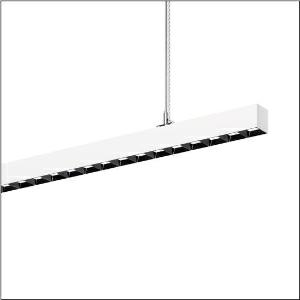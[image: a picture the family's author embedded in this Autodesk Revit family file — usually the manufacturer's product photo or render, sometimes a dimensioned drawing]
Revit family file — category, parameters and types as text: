
# Revit family: silica_r__21_51mx32dc3dwb_4ada
name_source: partatom
category: Lighting Fixtures
units: mm (PartAtom-declared; Revit-internal decimal feet)

## family parameters
Cut with Voids When Loaded = No
Host = Face
Light Source = No
Part Type = Normal
Room Calculation Point = No
Round Connector Dimension = Use Diameter
Shared = No

## types (1)
- --- (1 x LED, 18220 lm, 113 W, 3000K)
    Apparent Load = 113 VA
    CIE Flux Codes = 86 99 100 59 100
    Color Rendering = 80
    Color Temperature = 3000K
    Default Elevation = 1800 mm
    Description = Silica® 21, office luminaire, primary light control with darklight reflector, of PMMA, black, CAT 2 (L<= 3000cd/m²), light emission: direct/indirect distribution, primary light characteristic: symmetric, installation type: suspended mounting, LED, rated luminous flux: 18.220lm, luminous efficacy: 161lm/W, light colour: 830, colour temperature: 3000K, with terminal, 3+2-pole, max. 2.5mm², mains connection: 220..240V, AC, 50/60Hz, rated input power: 113W, luminaire housing, of aluminium, traffic white (RAL 9016), length: 3.004mm, width: 53mm, height: 53mm, protection rating (complete): IP20, insulation class (complete): insulation class I (protective earthing), certification: CE, permissible operating ambient temperature: 0..+35°C, standard: EN 50419, packaging unit: 1 piece
    Height = 53 mm
    Lamp = 1 x LED
    Lamp Light Flux = 18220 lm
    Lamp Power = 113 W
    Lamp count = 1
    Length = 3004 mm
    Luminous efficacy = 161 lm/W
    Manufacturer = Siteco
    ModVariant = No
    Model = 51MX32DC3DWB
    Mounting Place = Ceiling
    Mounting Type = Pendant
    Number of Poles = 1
    OnlyDefault = Yes
    Power Factor = 1
    Product Name = Silica® 21
    Product group = office luminaire | ceiling pendant
    ProductGroupID = 902
    Protection Class = Protection class I
    Protection Degree = IP 20
    RLX_Detail_Level = 1
    RLX_Emergency_Light_Flux = 0 lm
    RLX_Emergency_Type = 0
    RLX_Emergency_Type_DB = No
    RlxData = <blob elided: 64741 chars, md5=914d8fa5>
    Socket = socket
    Standby Power = 0 W
    System Light Flux = 18220 lm
    System Power = 113 W
    Type Comments = factory setting: luminous flux: 100 % | dim-lin: 254 | 391 mA
    Type Image = l_1335871.jpg
    URL = http://relux.com
    VarID = @adj_091697
    Voltage = 0 V
    Weight = 0.00 kg
    Width = 53 mm

## geometry (parser evidence)
native form markers: Blend x4, Sweep x13
no freeform markers — native parametric forms only
